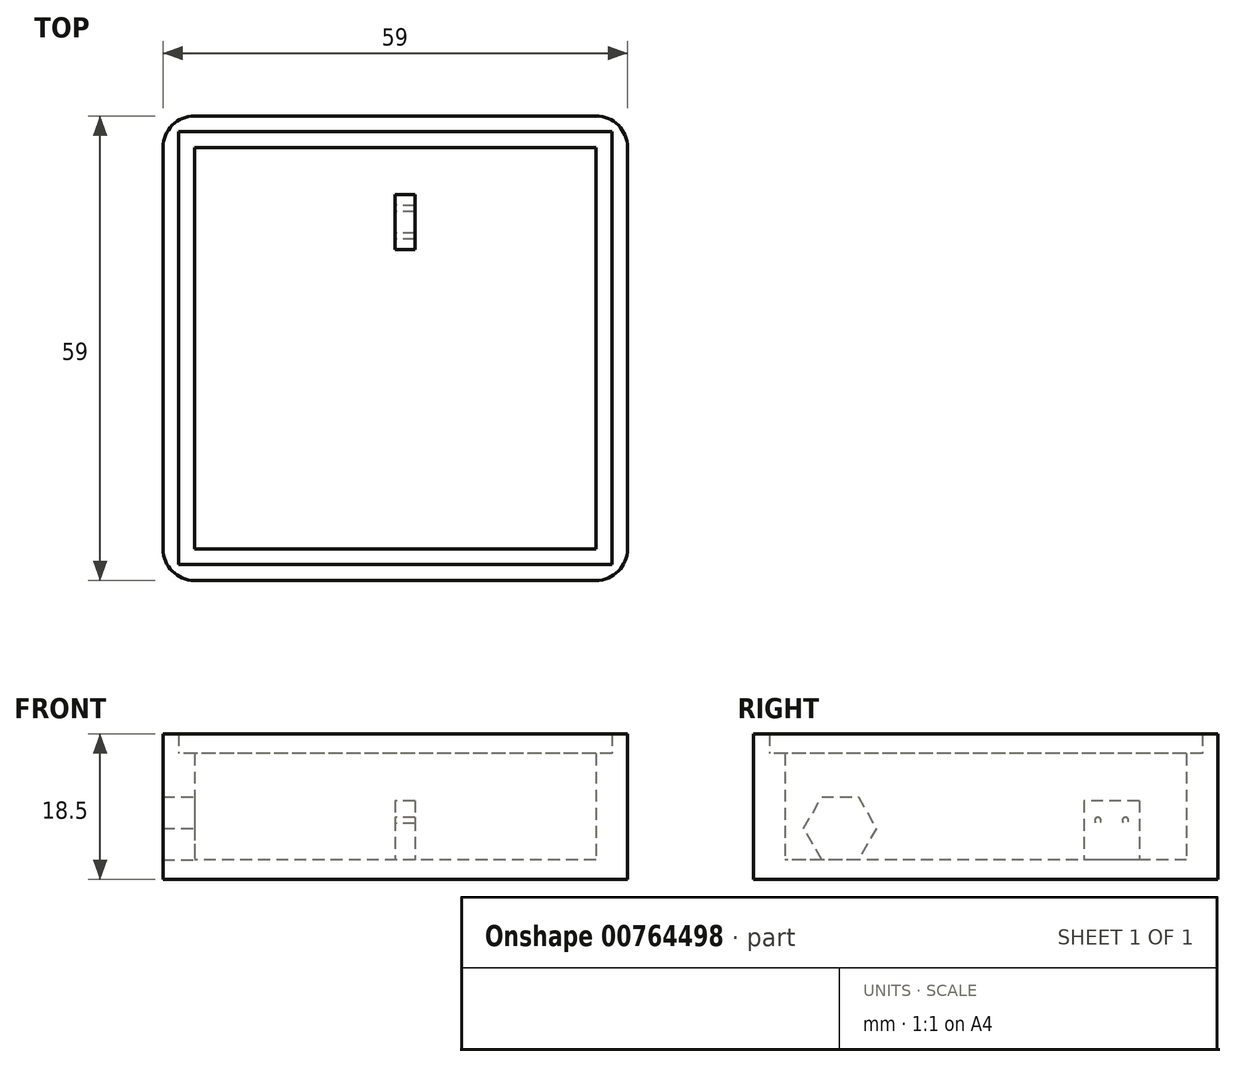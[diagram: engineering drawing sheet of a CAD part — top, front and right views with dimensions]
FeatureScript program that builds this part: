
annotation { "Feature Type Name" : "Feature", "Feature Type Description" : "" }
export const myFeature = defineFeature(function(context is Context, id is Id, definition is map)
    precondition{}
    {
        {
            var Q0;
            Q0=qCreatedBy(makeId("Top.planeOp"),FACE);
            var sketch = newSketch(context, id + "F0", { "sketchPlane" : qUnion([Q0])});
            skLineSegment(sketch, "E0.bottom", {"start": v(29.5, 29.5) * mm, "end": v(-29.5, 29.5) * mm});
            skLineSegment(sketch, "E0.top", {"start": v(29.5, -29.5) * mm, "end": v(-29.5, -29.5) * mm});
            skLineSegment(sketch, "E0.left", {"start": v(29.5, 29.5) * mm, "end": v(29.5, -29.5) * mm});
            skLineSegment(sketch, "E0.right", {"start": v(-29.5, 29.5) * mm, "end": v(-29.5, -29.5) * mm});
            skPoint(sketch, "E1", {"position": v(0, 29.5) * mm});
            skPoint(sketch, "E2", {"position": v(29.5, 0) * mm});
            skLineSegment(sketch, "E3.0", {"start": v(25.5, 25.5) * mm, "end": v(-25.5, 25.5) * mm});
            skLineSegment(sketch, "E3.1", {"start": v(25.5, 25.5) * mm, "end": v(25.5, -25.5) * mm});
            skLineSegment(sketch, "E3.2", {"start": v(25.5, -25.5) * mm, "end": v(-25.5, -25.5) * mm});
            skLineSegment(sketch, "E3.3", {"start": v(-25.5, 25.5) * mm, "end": v(-25.5, -25.5) * mm});
            skSolve(sketch);
        }
        {
            var Q0;
            Q0=qSketchRegion(id+"F0",true);
            extrude(context, id + "F1", {"entities" : qUnion([Q0]), "depth" : 16 * mm, "offsetDistance" : 25 * mm});
        }
        {
            var Q0;
            Q0=makeQuery(id+"F1.opExtrude","CAP_FACE",FACE,{"disambiguationData":[OSD([sQuery(id+"F0.wireOp",EDGE,"E0.bottom"),sQuery(id+"F0.wireOp",EDGE,"E0.top"),sQuery(id+"F0.wireOp",EDGE,"E0.left"),sQuery(id+"F0.wireOp",EDGE,"E0.right"),sQuery(id+"F0.wireOp",EDGE,"E3.0"),sQuery(id+"F0.wireOp",EDGE,"E3.1"),sQuery(id+"F0.wireOp",EDGE,"E3.2"),sQuery(id+"F0.wireOp",EDGE,"E3.3")])],"isStart":false});
            var sketch = newSketch(context, id + "F2", { "sketchPlane" : qUnion([Q0])});
            skLineSegment(sketch, "E4.bottom", {"start": v(29.5, 29.5) * mm, "end": v(-29.5, 29.5) * mm});
            skLineSegment(sketch, "E4.top", {"start": v(29.5, -29.5) * mm, "end": v(-29.5, -29.5) * mm});
            skLineSegment(sketch, "E4.left", {"start": v(29.5, 29.5) * mm, "end": v(29.5, -29.5) * mm});
            skLineSegment(sketch, "E4.right", {"start": v(-29.5, 29.5) * mm, "end": v(-29.5, -29.5) * mm});
            skLineSegment(sketch, "E5.0", {"start": v(27.5, -27.5) * mm, "end": v(-27.5, -27.5) * mm});
            skLineSegment(sketch, "E5.1", {"start": v(27.5, 27.5) * mm, "end": v(27.5, -27.5) * mm});
            skLineSegment(sketch, "E5.2", {"start": v(27.5, 27.5) * mm, "end": v(-27.5, 27.5) * mm});
            skLineSegment(sketch, "E5.3", {"start": v(-27.5, 27.5) * mm, "end": v(-27.5, -27.5) * mm});
            skSolve(sketch);
        }
        {
            var Q0;
            Q0=qSketchRegion(id+"F2",true);
            extrude(context, id + "F3", {"entities" : qUnion([Q0]), "operationType" : NewBodyOperationType.ADD, "depth" : 2.5 * mm, "offsetDistance" : 25 * mm});
        }
        {
            var Q0;
            Q0=makeQuery(id+"F1.opExtrude","CAP_FACE",FACE,{"disambiguationData":[OSD([sQuery(id+"F0.wireOp",EDGE,"E0.bottom"),sQuery(id+"F0.wireOp",EDGE,"E0.top"),sQuery(id+"F0.wireOp",EDGE,"E0.left"),sQuery(id+"F0.wireOp",EDGE,"E0.right"),sQuery(id+"F0.wireOp",EDGE,"E3.0"),sQuery(id+"F0.wireOp",EDGE,"E3.1"),sQuery(id+"F0.wireOp",EDGE,"E3.2"),sQuery(id+"F0.wireOp",EDGE,"E3.3")])],"isStart":true});
            var sketch = newSketch(context, id + "F4", { "sketchPlane" : qUnion([Q0])});
            skLineSegment(sketch, "E6.bottom", {"start": v(25.5, -25.5) * mm, "end": v(-25.5, -25.5) * mm});
            skLineSegment(sketch, "E6.top", {"start": v(25.5, 25.5) * mm, "end": v(-25.5, 25.5) * mm});
            skLineSegment(sketch, "E6.left", {"start": v(25.5, -25.5) * mm, "end": v(25.5, 25.5) * mm});
            skLineSegment(sketch, "E6.right", {"start": v(-25.5, -25.5) * mm, "end": v(-25.5, 25.5) * mm});
            skSolve(sketch);
        }
        {
            var Q0;
            Q0=qSketchRegion(id+"F4",true);
            extrude(context, id + "F5", {"entities" : qUnion([Q0]), "operationType" : NewBodyOperationType.ADD, "oppositeDirection" : true, "depth" : 2.5 * mm, "offsetDistance" : 25 * mm});
        }
        {
            var Q0;
            Q0=makeQuery(id+"F1.opExtrude","SWEPT_FACE",FACE,{"disambiguationData":[OSD([sQuery(id+"F0.wireOp",EDGE,"E3.1")])]});
            var sketch = newSketch(context, id + "F6", { "sketchPlane" : qUnion([Q0])});
            skCircle(sketch, "E7.cCircle", {"center": v(18.5, 6.5) * mm, "radius": 4 * mm, "construction": true});
            skLineSegment(sketch, "E7.0", {"start": v(13.88, 6.5) * mm, "end": v(16.2, 10.5) * mm});
            skLineSegment(sketch, "E7.1", {"start": v(16.2, 10.5) * mm, "end": v(20.8, 10.5) * mm});
            skLineSegment(sketch, "E7.2", {"start": v(20.8, 10.5) * mm, "end": v(23.12, 6.5) * mm});
            skLineSegment(sketch, "E7.3", {"start": v(23.12, 6.5) * mm, "end": v(20.8, 2.5) * mm});
            skLineSegment(sketch, "E7.4", {"start": v(20.8, 2.5) * mm, "end": v(16.2, 2.5) * mm});
            skLineSegment(sketch, "E7.5", {"start": v(16.2, 2.5) * mm, "end": v(13.88, 6.5) * mm});
            skPoint(sketch, "E7.0.midPoint", {"position": v(15.04, 8.5) * mm});
            skSolve(sketch);
        }
        {
            var Q0;
            Q0=makeQuery(id+"F0.imprint","IMPRINT",FACE,{"disambiguationData":[TD([[makeQuery(id+"F0.imprint","IMPRINT",EDGE,{"derivedFrom":sQuery(id+"F0.wireOp",EDGE,"E3.0")}),1.0]])]});
            var sketch = newSketch(context, id + "F7", { "sketchPlane" : qUnion([Q0])});
            skLineSegment(sketch, "E8.bottom", {"start": v(2.5, 19.5) * mm, "end": v(0, 19.5) * mm});
            skLineSegment(sketch, "E8.top", {"start": v(2.5, 12.5) * mm, "end": v(0, 12.5) * mm});
            skLineSegment(sketch, "E8.left", {"start": v(2.5, 19.5) * mm, "end": v(2.5, 12.5) * mm});
            skLineSegment(sketch, "E8.right", {"start": v(0, 19.5) * mm, "end": v(0, 12.5) * mm});
            skSolve(sketch);
        }
        {
            var Q0;
            Q0 = qSketchRegion(id + "F7", true);
            extrude(context, id + "F8", {"entities" : qUnion([Q0]), "operationType" : NewBodyOperationType.ADD, "depth" : 10 * mm, "offsetDistance" : 25 * mm});
        }
        {
            var Q0;
            Q0=makeQuery(id+"F8.opExtrude","SWEPT_FACE",FACE,{"disambiguationData":[OSD([sQuery(id+"F7.wireOp",EDGE,"E8.right")])]});
            var sketch = newSketch(context, id + "F9", { "sketchPlane" : qUnion([Q0])});
            skCircle(sketch, "E9", {"center": v(-17.75, 7.5) * mm, "radius": 0.4 * mm});
            skLineSegment(sketch, "E10", {"start": v(-16, 2.5) * mm, "end": v(-16, 10) * mm, "construction": true});
            skLineSegment(sketch, "E11", {"start": v(-16, 2.5) * mm, "end": v(-19.5, 2.5) * mm, "construction": true});
            skLineSegment(sketch, "E12", {"start": v(-17.75, 2.5) * mm, "end": v(-17.75, 10) * mm, "construction": true});
            skCircle(sketch, "E13.MirrorC", {"center": v(-14.25, 7.5) * mm, "radius": 0.4 * mm});
            skSolve(sketch);
        }
        {
            var Q0;
            Q0 = qSketchRegion(id + "F9", true);
            extrude(context, id + "F10", {"entities" : qUnion([Q0]), "operationType" : NewBodyOperationType.REMOVE, "oppositeDirection" : true, "depth" : 2.5 * mm, "offsetDistance" : 25 * mm, "hasDraft" : true, "draftAngle" : 0.25 * degree, "draftPullDirection" : true});
        }
        {
            var Q0;
            Q0=makeQuery(id+"F3.boolean.opBoolean","MERGE",EDGE,{"derivedFrom":[makeQuery(id+"F1.opExtrude","SWEPT_EDGE",EDGE,{"disambiguationData":[OSD([sQuery(id+"F0.wireOp",EDGE,"E0.bottom"),sQuery(id+"F0.wireOp",EDGE,"E0.left")])]}),makeQuery(id+"F3.opExtrude","SWEPT_EDGE",EDGE,{"disambiguationData":[OSD([sQuery(id+"F2.wireOp",EDGE,"E4.bottom"),sQuery(id+"F2.wireOp",EDGE,"E4.left")])]})]});
            fillet(context, id + "F11", {"entities" : qUnion([Q0]), "radius" : 4 * mm, "tangentPropagation" : true, "allowEdgeOverflow" : false});
        }
        {
            var Q0;
            Q0=makeQuery(id+"F3.boolean.opBoolean","MERGE",EDGE,{"derivedFrom":[makeQuery(id+"F1.opExtrude","SWEPT_EDGE",EDGE,{"disambiguationData":[OSD([sQuery(id+"F0.wireOp",EDGE,"E0.bottom"),sQuery(id+"F0.wireOp",EDGE,"E0.right")])]}),makeQuery(id+"F3.opExtrude","SWEPT_EDGE",EDGE,{"disambiguationData":[OSD([sQuery(id+"F2.wireOp",EDGE,"E4.bottom"),sQuery(id+"F2.wireOp",EDGE,"E4.right")])]})]});
            var Q1;
            Q1=makeQuery(id+"F3.boolean.opBoolean","MERGE",EDGE,{"derivedFrom":[makeQuery(id+"F1.opExtrude","SWEPT_EDGE",EDGE,{"disambiguationData":[OSD([sQuery(id+"F0.wireOp",EDGE,"E0.top"),sQuery(id+"F0.wireOp",EDGE,"E0.right")])]}),makeQuery(id+"F3.opExtrude","SWEPT_EDGE",EDGE,{"disambiguationData":[OSD([sQuery(id+"F2.wireOp",EDGE,"E4.top"),sQuery(id+"F2.wireOp",EDGE,"E4.right")])]})]});
            var Q2;
            Q2=makeQuery(id+"F3.boolean.opBoolean","MERGE",EDGE,{"derivedFrom":[makeQuery(id+"F1.opExtrude","SWEPT_EDGE",EDGE,{"disambiguationData":[OSD([sQuery(id+"F0.wireOp",EDGE,"E0.top"),sQuery(id+"F0.wireOp",EDGE,"E0.left")])]}),makeQuery(id+"F3.opExtrude","SWEPT_EDGE",EDGE,{"disambiguationData":[OSD([sQuery(id+"F2.wireOp",EDGE,"E4.top"),sQuery(id+"F2.wireOp",EDGE,"E4.left")])]})]});
            fillet(context, id + "F12", {"entities" : qUnion([Q0, Q1, Q2]), "radius" : 4 * mm, "tangentPropagation" : true, "allowEdgeOverflow" : false});
        }
        {
            var Q0;
            Q0=makeQuery(id+"F1.opExtrude","SWEPT_FACE",FACE,{"disambiguationData":[OSD([sQuery(id+"F0.wireOp",EDGE,"E3.3")])]});
            var sketch = newSketch(context, id + "F13", { "sketchPlane" : qUnion([Q0])});
            skCircle(sketch, "E14.cCircle", {"center": v(-18.5, 6.5) * mm, "radius": 4 * mm, "construction": true});
            skLineSegment(sketch, "E14.0", {"start": v(-13.88, 6.5) * mm, "end": v(-16.2, 2.5) * mm});
            skLineSegment(sketch, "E14.1", {"start": v(-16.2, 2.5) * mm, "end": v(-20.8, 2.5) * mm});
            skLineSegment(sketch, "E14.2", {"start": v(-20.8, 2.5) * mm, "end": v(-23.12, 6.5) * mm});
            skLineSegment(sketch, "E14.3", {"start": v(-23.12, 6.5) * mm, "end": v(-20.8, 10.5) * mm});
            skLineSegment(sketch, "E14.4", {"start": v(-20.8, 10.5) * mm, "end": v(-16.2, 10.5) * mm});
            skLineSegment(sketch, "E14.5", {"start": v(-16.2, 10.5) * mm, "end": v(-13.88, 6.5) * mm});
            skPoint(sketch, "E14.0.midPoint", {"position": v(-15.04, 4.5) * mm});
            skSolve(sketch);
        }
        {
            var Q0;
            Q0 = qSketchRegion(id + "F13", true);
            extrude(context, id + "F14", {"entities" : qUnion([Q0]), "operationType" : NewBodyOperationType.REMOVE, "oppositeDirection" : true, "depth" : 25 * mm, "offsetDistance" : 25 * mm});
        }
    });
